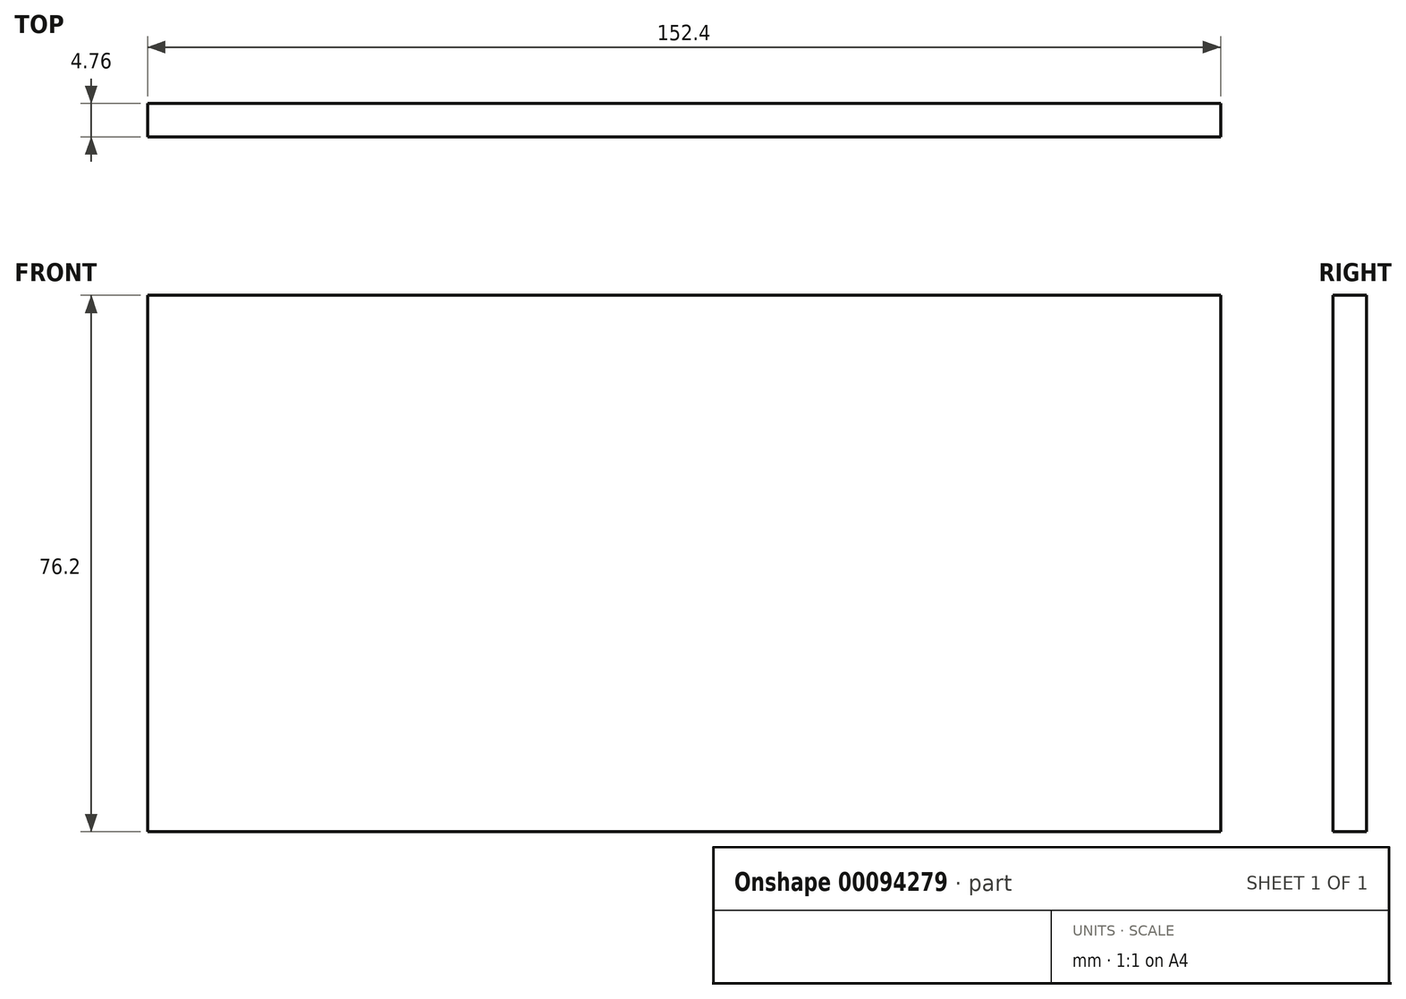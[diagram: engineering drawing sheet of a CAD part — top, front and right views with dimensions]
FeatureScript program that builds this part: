
annotation { "Feature Type Name" : "Feature", "Feature Type Description" : "" }
export const myFeature = defineFeature(function(context is Context, id is Id, definition is map)
    precondition{}
    {
        {
            var Q0;
            Q0=qCreatedBy(makeId("Front.planeOp"),FACE);
            var sketch = newSketch(context, id + "F0", { "sketchPlane" : qUnion([Q0])});
            skLineSegment(sketch, "E0.bottom", {"start": v(76.2, 38.1) * mm, "end": v(-76.2, 38.1) * mm});
            skLineSegment(sketch, "E0.top", {"start": v(76.2, -38.1) * mm, "end": v(-76.2, -38.1) * mm});
            skLineSegment(sketch, "E0.left", {"start": v(76.2, 38.1) * mm, "end": v(76.2, -38.1) * mm});
            skLineSegment(sketch, "E0.right", {"start": v(-76.2, 38.1) * mm, "end": v(-76.2, -38.1) * mm});
            skPoint(sketch, "E0.middle", {"position": v(0, 0) * mm});
            skSolve(sketch);
        }
        {
            var Q0;
            Q0 = qSketchRegion(id + "F0", true);
            extrude(context, id + "F1", {"entities" : qUnion([Q0]), "depth" : 4.76 * mm});
        }
    });
